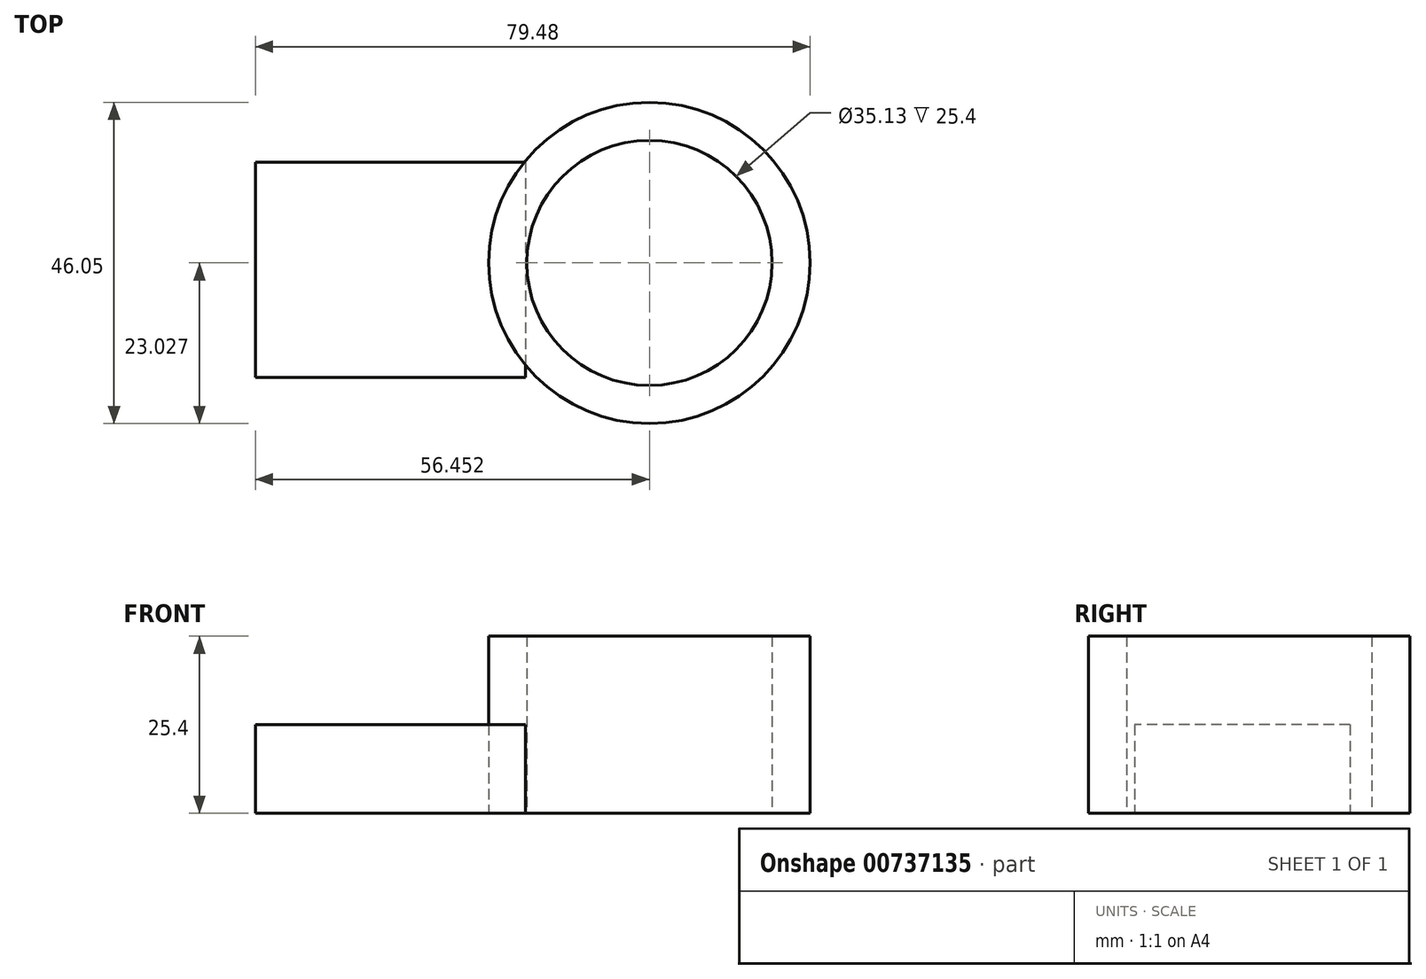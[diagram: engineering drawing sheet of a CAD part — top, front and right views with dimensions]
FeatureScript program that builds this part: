
annotation { "Feature Type Name" : "Feature", "Feature Type Description" : "" }
export const myFeature = defineFeature(function(context is Context, id is Id, definition is map)
    precondition{}
    {
        {
            var Q0;
            Q0=qCreatedBy(makeId("Top.planeOp"),FACE);
            var sketch = newSketch(context, id + "F0", { "sketchPlane" : qUnion([Q0])});
            skLineSegment(sketch, "E0.bottom", {"start": v(-33.43, 14.9) * mm, "end": v(5.27, 14.9) * mm});
            skLineSegment(sketch, "E0.top", {"start": v(-33.43, -15.98) * mm, "end": v(5.27, -15.98) * mm});
            skLineSegment(sketch, "E0.left", {"start": v(-33.43, 14.9) * mm, "end": v(-33.43, -15.98) * mm});
            skLineSegment(sketch, "E0.right", {"start": v(5.27, 14.9) * mm, "end": v(5.27, -15.98) * mm});
            skCircle(sketch, "E1", {"center": v(23.02, 0.46) * mm, "radius": 23.03 * mm});
            skPoint(sketch, "E1.first.point", {"position": v(0, 0) * mm});
            skPoint(sketch, "E1.second.point", {"position": v(30.74, 22.15) * mm});
            skPoint(sketch, "E1.third.point", {"position": v(43.36, -10.34) * mm});
            skCircle(sketch, "E2", {"center": v(23.02, 0.46) * mm, "radius": 17.57 * mm});
            skSolve(sketch);
        }
        {
            var Q0;
            {var subQ1=sQuery(id+"F0.wireOp",EDGE,"E0.top");Q0=makeQuery(id+"F0.imprint","IMPRINT",FACE,{"disambiguationData":[TD([[makeQuery(id+"F0.imprint","IMPRINT",EDGE,{"derivedFrom":subQ1}),1.0]])]});}
            var Q1;
            {var subQ0=sQuery(id+"F0.wireOp",EDGE,"E0.right");var subQ1=sQuery(id+"F0.wireOp",EDGE,"E0.bottom");var subQ2=makeQuery(id+"F0.imprint","INTERSECT",VERTEX,{"derivedFrom":[subQ1,subQ0]});Q1=makeQuery(id+"F0.imprint","IMPRINT",FACE,{"disambiguationData":[TD([[makeQuery(id+"F0.imprint","IMPRINT",EDGE,{"disambiguationData":[TD([[subQ2,1.0]])],"derivedFrom":subQ1}),-1.0]])]});}
            extrude(context, id + "F1", {"entities" : qUnion([Q0, Q1]), "depth" : 12.7 * mm, "offsetDistance" : 25.4 * mm});
        }
        {
            var Q0;
            Q0=makeQuery(id+"F0.imprint","IMPRINT",FACE,{"disambiguationData":[TD([[makeQuery(id+"F0.imprint","IMPRINT",EDGE,{"derivedFrom":sQuery(id+"F0.wireOp",EDGE,"E2")}),-1.0]])]});
            var Q1;
            {var subQ0=sQuery(id+"F0.wireOp",EDGE,"E0.right");var subQ1=sQuery(id+"F0.wireOp",EDGE,"E0.bottom");var subQ2=makeQuery(id+"F0.imprint","INTERSECT",VERTEX,{"derivedFrom":[subQ1,subQ0]});Q1=makeQuery(id+"F0.imprint","IMPRINT",FACE,{"disambiguationData":[TD([[makeQuery(id+"F0.imprint","IMPRINT",EDGE,{"disambiguationData":[TD([[subQ2,1.0]])],"derivedFrom":subQ1}),-1.0]])]});}
            extrude(context, id + "F2", {"entities" : qUnion([Q0, Q1]), "depth" : 25.4 * mm, "offsetDistance" : 25.4 * mm});
        }
    });
